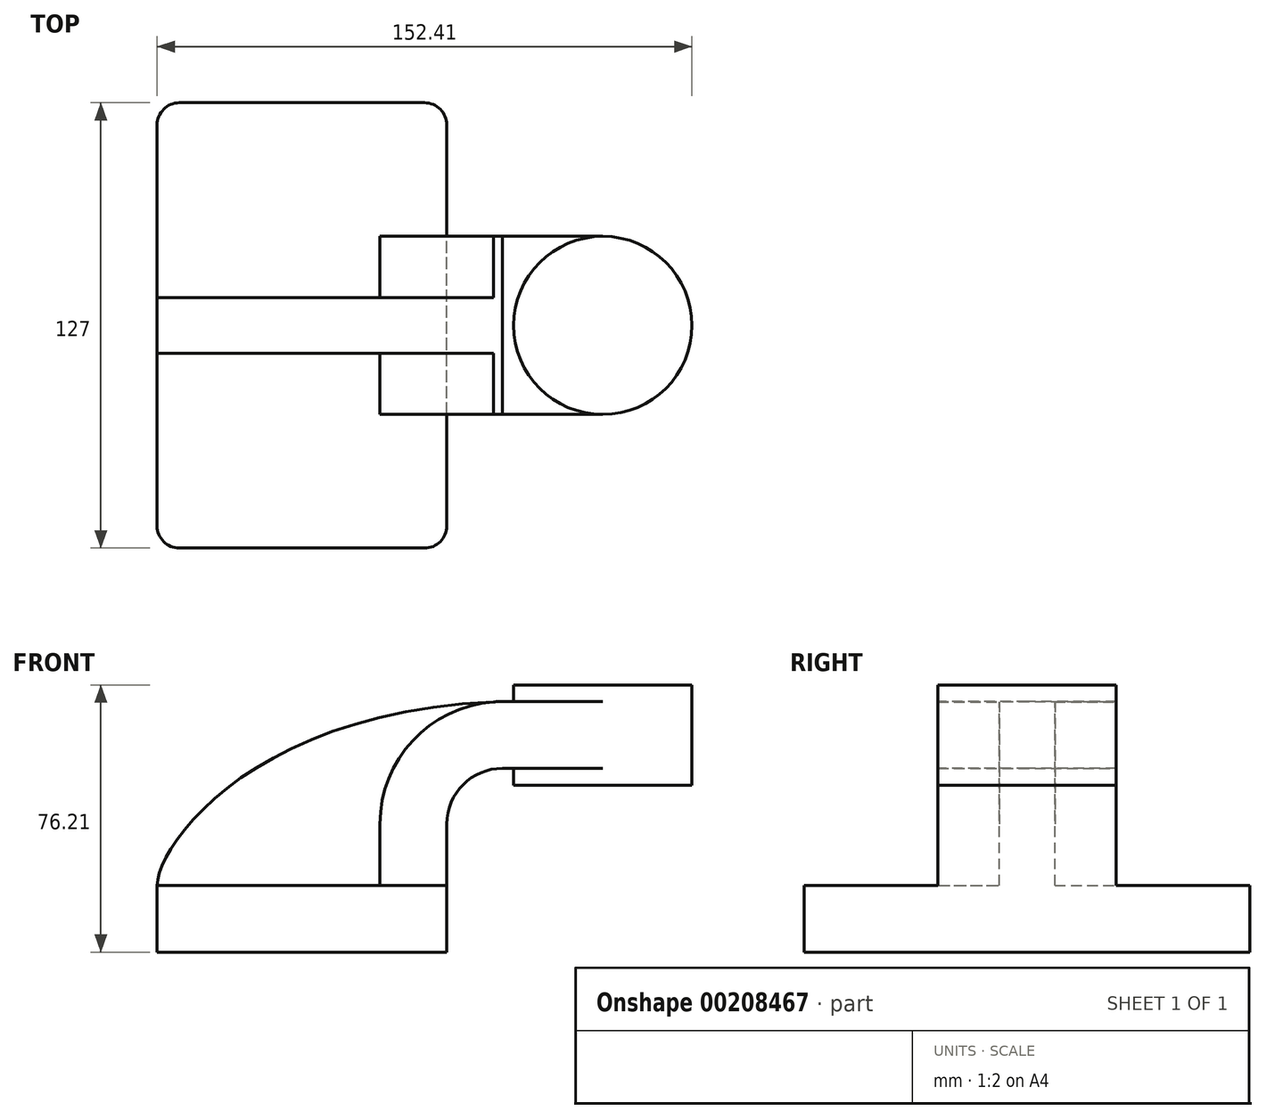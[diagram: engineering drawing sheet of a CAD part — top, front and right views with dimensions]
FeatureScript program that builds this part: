
annotation { "Feature Type Name" : "Feature", "Feature Type Description" : "" }
export const myFeature = defineFeature(function(context is Context, id is Id, definition is map)
    precondition{}
    {
        {
            var Q0;
            Q0=qCreatedBy(makeId("Front.planeOp"),FACE);
            var sketch = newSketch(context, id + "F0", { "sketchPlane" : qUnion([Q0])});
            skLineSegment(sketch, "E0.bottom", {"start": v(111.12, 38.1) * mm, "end": v(60.32, 38.1) * mm});
            skLineSegment(sketch, "E0.top", {"start": v(111.12, 66.68) * mm, "end": v(60.32, 66.67) * mm});
            skLineSegment(sketch, "E0.left", {"start": v(111.12, 38.1) * mm, "end": v(111.12, 66.67) * mm});
            skLineSegment(sketch, "E0.right", {"start": v(60.32, 38.1) * mm, "end": v(60.32, 66.67) * mm});
            skPoint(sketch, "E0.middle", {"position": v(85.73, 52.39) * mm});
            skLineSegment(sketch, "E1", {"start": v(41.27, 9.53) * mm, "end": v(41.27, 27) * mm});
            skArc(sketch, "E2", {"start": v(41.27, 27) * mm, "mid": v(45.92, 38.23) * mm, "end": v(57.15, 42.88) * mm});
            skLineSegment(sketch, "E3", {"start": v(57.15, 42.88) * mm, "end": v(85.73, 42.88) * mm});
            skLineSegment(sketch, "E4.bottom", {"start": v(41.28, -9.52) * mm, "end": v(-41.27, -9.53) * mm});
            skLineSegment(sketch, "E4.top", {"start": v(41.27, 9.53) * mm, "end": v(-41.28, 9.53) * mm});
            skLineSegment(sketch, "E4.left", {"start": v(41.28, -9.52) * mm, "end": v(41.27, 9.53) * mm});
            skLineSegment(sketch, "E4.right", {"start": v(-41.28, -9.53) * mm, "end": v(-41.28, 9.52) * mm});
            skPoint(sketch, "E4.middle", {"position": v(0, 0) * mm});
            skLineSegment(sketch, "E5.0", {"start": v(57.15, 61.93) * mm, "end": v(85.72, 61.93) * mm});
            skArc(sketch, "E5.1", {"start": v(22.22, 27) * mm, "mid": v(32.45, 51.7) * mm, "end": v(57.15, 61.93) * mm});
            skLineSegment(sketch, "E5.2", {"start": v(22.22, 9.53) * mm, "end": v(22.22, 27) * mm});
            skLineSegment(sketch, "E6", {"start": v(85.72, 38.1) * mm, "end": v(85.72, 66.68) * mm});
            skFitSpline(sketch, "E7", {"points": [v(-41.28, 9.53) * mm, v(57.15, 61.93) * mm], "startDerivative": vector(0.24, 33.57) * mm, "endDerivative": vector(214.6, 6.55) * mm});
            skSolve(sketch);
        }
        {
            var Q0;
            Q0=makeQuery(id+"F0.imprint","IMPRINT",FACE,{"disambiguationData":[TD([[makeQuery(id+"F0.imprint","IMPRINT",EDGE,{"derivedFrom":sQuery(id+"F0.wireOp",EDGE,"E4.bottom")}),-1.0]])]});
            extrude(context, id + "F1", {"entities" : qUnion([Q0]), "endBound" : BoundingType.SYMMETRIC, "depth" : 127 * mm});
        }
        {
            var Q0;
            {var subQ4=sQuery(id+"F0.wireOp",EDGE,"E1");Q0=makeQuery(id+"F0.imprint","IMPRINT",FACE,{"disambiguationData":[TD([[makeQuery(id+"F0.imprint","IMPRINT",EDGE,{"derivedFrom":subQ4}),1.0]])]});}
            var Q1;
            {var subQ0=sQuery(id+"F0.wireOp",EDGE,"E3");var subQ1=sQuery(id+"F0.wireOp",EDGE,"E0.right");var subQ2=makeQuery(id+"F0.imprint","INTERSECT",VERTEX,{"derivedFrom":[subQ1,subQ0]});Q1=makeQuery(id+"F0.imprint","IMPRINT",FACE,{"disambiguationData":[TD([[makeQuery(id+"F0.imprint","IMPRINT",EDGE,{"disambiguationData":[TD([[subQ2,-1.0]])],"derivedFrom":subQ1}),-1.0]])]});}
            extrude(context, id + "F2", {"entities" : qUnion([Q0, Q1]), "operationType" : NewBodyOperationType.ADD, "endBound" : BoundingType.SYMMETRIC, "depth" : 50.8 * mm});
        }
        {
            var Q0;
            {var subQ3=sQuery(id+"F0.wireOp",EDGE,"E5.2");Q0=makeQuery(id+"F0.imprint","IMPRINT",FACE,{"disambiguationData":[TD([[makeQuery(id+"F0.imprint","IMPRINT",EDGE,{"derivedFrom":subQ3}),1.0]])]});}
            extrude(context, id + "F3", {"entities" : qUnion([Q0]), "operationType" : NewBodyOperationType.ADD, "endBound" : BoundingType.SYMMETRIC, "depth" : 15.88 * mm});
        }
        {
            var Q0;
            {var subQ4=sQuery(id+"F0.wireOp",EDGE,"E0.left");Q0=makeQuery(id+"F0.imprint","IMPRINT",FACE,{"disambiguationData":[TD([[makeQuery(id+"F0.imprint","IMPRINT",EDGE,{"derivedFrom":subQ4}),1.0]])]});}
            var Q1;
            Q1=sQuery(id+"F0.wireOp",EDGE,"E6");
            revolve(context, id + "F4", {"operationType" : NewBodyOperationType.ADD, "entities" : qUnion([Q0]), "axis" : qUnion([Q1]), "revolveType" : RevolveType.FULL});
        }
        {
            var Q0;
            Q0=makeQuery(id+"F1.opExtrude","CAP_EDGE",EDGE,{"disambiguationData":[OSD([sQuery(id+"F0.wireOp",EDGE,"E4.left")])],"isStart":false});
            var Q1;
            Q1=makeQuery(id+"F1.opExtrude","CAP_EDGE",EDGE,{"disambiguationData":[OSD([sQuery(id+"F0.wireOp",EDGE,"E4.right")])],"isStart":false});
            var Q2;
            Q2=makeQuery(id+"F1.opExtrude","CAP_EDGE",EDGE,{"disambiguationData":[OSD([sQuery(id+"F0.wireOp",EDGE,"E4.left")])],"isStart":true});
            var Q3;
            Q3=makeQuery(id+"F1.opExtrude","CAP_EDGE",EDGE,{"disambiguationData":[OSD([sQuery(id+"F0.wireOp",EDGE,"E4.right")])],"isStart":true});
            fillet(context, id + "F5", {"entities" : qUnion([Q0, Q1, Q2, Q3]), "radius" : 6.35 * mm, "tangentPropagation" : true, "allowEdgeOverflow" : false});
        }
    });
